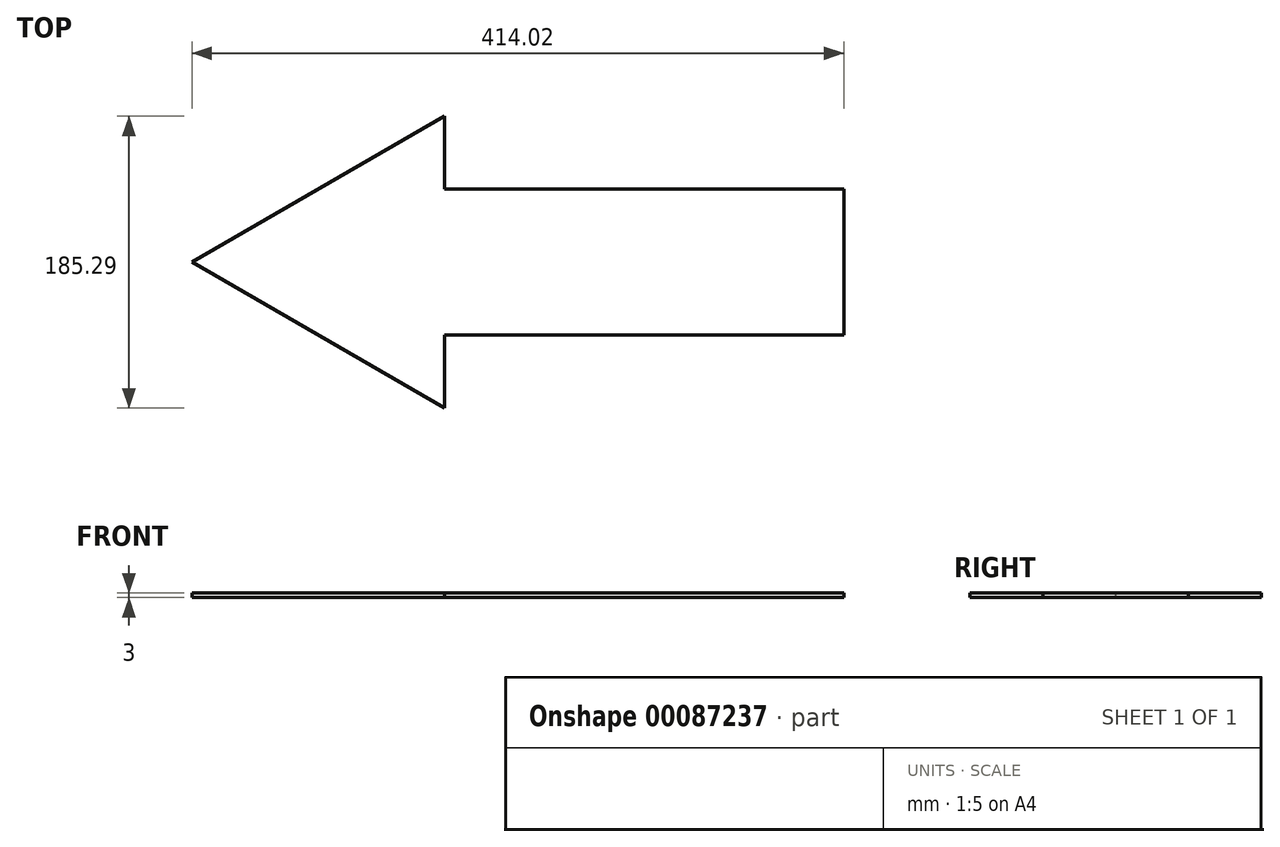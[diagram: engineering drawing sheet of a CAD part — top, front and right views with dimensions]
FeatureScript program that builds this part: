
annotation { "Feature Type Name" : "Feature", "Feature Type Description" : "" }
export const myFeature = defineFeature(function(context is Context, id is Id, definition is map)
    precondition{}
    {
        {
            var Q0;
            Q0=qCreatedBy(makeId("Top.planeOp"),FACE);
            var sketch = newSketch(context, id + "F0", { "sketchPlane" : qUnion([Q0])});
            skLineSegment(sketch, "E0.0", {"start": v(92.64, -53.49) * mm, "end": v(-92.64, -53.49) * mm});
            skLineSegment(sketch, "E0.1", {"start": v(-92.64, -53.49) * mm, "end": v(0, 106.97) * mm});
            skLineSegment(sketch, "E0.2", {"start": v(0, 106.97) * mm, "end": v(23.16, 66.86) * mm});
            skPoint(sketch, "E0.0.midPoint", {"position": v(0, -53.49) * mm});
            skLineSegment(sketch, "E1", {"start": v(23.16, 66.86) * mm, "end": v(126.88, 126.74) * mm});
            skPoint(sketch, "E2.orphan", {"position": v(-46.32, 26.74) * mm});
            skLineSegment(sketch, "E3.trimOffspring", {"start": v(69.48, -13.37) * mm, "end": v(173.2, 46.51) * mm});
            skLineSegment(sketch, "E4.trimOffspring", {"start": v(69.48, -13.37) * mm, "end": v(92.64, -53.49) * mm});
            skPoint(sketch, "E0.cCircle.center.orphan", {"position": v(0, 0) * mm});
            skLineSegment(sketch, "E5", {"start": v(126.88, 126.74) * mm, "end": v(242.75, 193.64) * mm});
            skLineSegment(sketch, "E6", {"start": v(242.75, 193.64) * mm, "end": v(285.8, 119.07) * mm});
            skLineSegment(sketch, "E7", {"start": v(173.2, 46.51) * mm, "end": v(289.07, 113.4) * mm});
            skLineSegment(sketch, "E8", {"start": v(285.8, 119.07) * mm, "end": v(289.07, 113.4) * mm});
            skSolve(sketch);
        }
        {
            var Q0;
            Q0=makeQuery(id+"F0.imprint","IMPRINT",FACE,{"disambiguationData":[TD([[makeQuery(id+"F0.imprint","IMPRINT",EDGE,{"derivedFrom":sQuery(id+"F0.wireOp",EDGE,"E0.0")}),-1.0]])]});
            extrude(context, id + "F1", {"entities" : qUnion([Q0]), "depth" : 3 * mm});
        }
        {
            var Q0;
            Q0=makeQuery(id+"F1.opExtrude","SWEPT_BODY",BODY,{"disambiguationData":[OSD([sQuery(id+"F0.wireOp",EDGE,"E0.0"),sQuery(id+"F0.wireOp",EDGE,"E0.1"),sQuery(id+"F0.wireOp",EDGE,"E0.2"),sQuery(id+"F0.wireOp",EDGE,"E1"),sQuery(id+"F0.wireOp",EDGE,"E3.trimOffspring"),sQuery(id+"F0.wireOp",EDGE,"E4.trimOffspring"),sQuery(id+"F0.wireOp",EDGE,"E5"),sQuery(id+"F0.wireOp",EDGE,"E6"),sQuery(id+"F0.wireOp",EDGE,"E7"),sQuery(id+"F0.wireOp",EDGE,"E8")])]});
            var Q1;
            Q1=makeQuery(id+"F1.opExtrude","SWEPT_EDGE",EDGE,{"disambiguationData":[OSD([sQuery(id+"F0.wireOp",EDGE,"E0.0"),sQuery(id+"F0.wireOp",EDGE,"E4.trimOffspring")])]});
            transform(context, id + "F2", {"entities" : qUnion([Q0]), "transformType" : TransformType.ROTATION, "transformAxis" : qUnion([Q1]), "angle" : 30 * degree, "makeCopy" : false});
        }
    });
